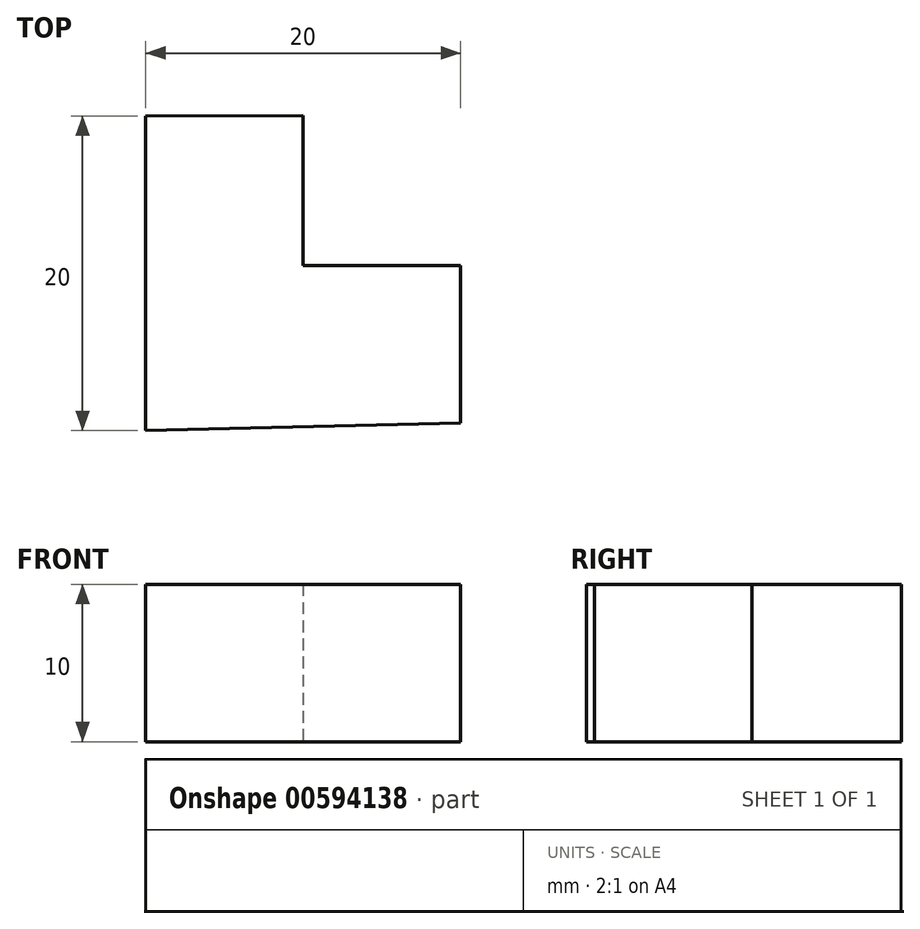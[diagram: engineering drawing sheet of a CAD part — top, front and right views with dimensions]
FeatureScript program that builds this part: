
annotation { "Feature Type Name" : "Feature", "Feature Type Description" : "" }
export const myFeature = defineFeature(function(context is Context, id is Id, definition is map)
    precondition{}
    {
        {
            var Q0;
            Q0=qCreatedBy(makeId("Top.planeOp"),FACE);
            var sketch = newSketch(context, id + "F0", { "sketchPlane" : qUnion([Q0])});
            skLineSegment(sketch, "E0", {"start": v(-61.78, 18.48) * mm, "end": v(-61.78, -1.52) * mm});
            skLineSegment(sketch, "E1", {"start": v(-41.78, -1.03) * mm, "end": v(-41.78, 8.97) * mm});
            skLineSegment(sketch, "E2", {"start": v(-41.78, 8.97) * mm, "end": v(-51.78, 8.97) * mm});
            skLineSegment(sketch, "E3", {"start": v(-51.78, 8.97) * mm, "end": v(-51.78, 18.48) * mm});
            skLineSegment(sketch, "E4", {"start": v(-51.78, 18.48) * mm, "end": v(-61.78, 18.48) * mm});
            skLineSegment(sketch, "E5", {"start": v(-61.78, -1.52) * mm, "end": v(-41.78, -1.03) * mm});
            skSolve(sketch);
        }
        {
            var Q0;
            Q0=makeQuery(id+"F0.imprint","IMPRINT",FACE,{"disambiguationData":[TD([[makeQuery(id+"F0.imprint","IMPRINT",EDGE,{"derivedFrom":sQuery(id+"F0.wireOp",EDGE,"E0")}),1.0]])]});
            extrude(context, id + "F1", {"entities" : qUnion([Q0]), "depth" : 10 * mm, "offsetDistance" : 25 * mm});
        }
    });
